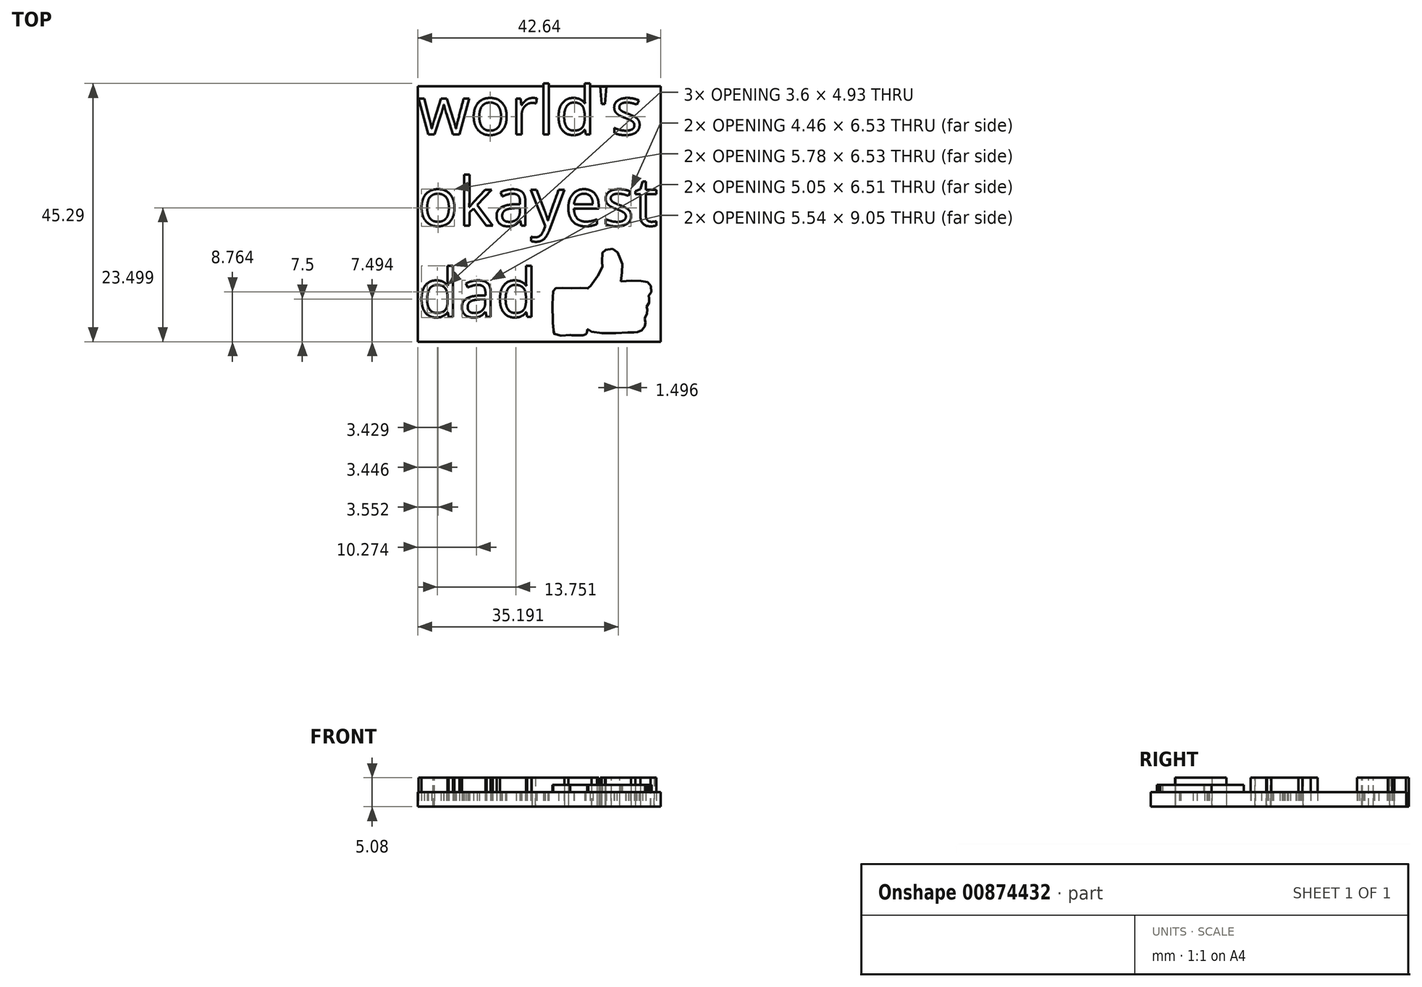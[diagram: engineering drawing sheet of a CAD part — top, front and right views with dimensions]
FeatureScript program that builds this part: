
annotation { "Feature Type Name" : "Feature", "Feature Type Description" : "" }
export const myFeature = defineFeature(function(context is Context, id is Id, definition is map)
    precondition{}
    {
        {
            var Q0;
            Q0=qCreatedBy(makeId("Top.planeOp"),FACE);
            var sketch = newSketch(context, id + "F0", { "sketchPlane" : qUnion([Q0])});
            skLineSegment(sketch, "E0.bottom", {"start": v(-21.32, 22.41) * mm, "end": v(21.32, 22.41) * mm});
            skLineSegment(sketch, "E0.top", {"start": v(-21.32, -22.41) * mm, "end": v(21.32, -22.41) * mm});
            skLineSegment(sketch, "E0.left", {"start": v(-21.32, 22.41) * mm, "end": v(-21.32, -22.41) * mm});
            skLineSegment(sketch, "E0.right", {"start": v(21.32, 22.41) * mm, "end": v(21.32, -22.41) * mm});
            skPoint(sketch, "E0.middle", {"position": v(0, 0) * mm});
            skText(sketch, "E1", { "text": "world\'s \nokayest \ndad", "fontName": "OpenSans-Regular.ttf"});
            const initialGuessF0  = {"E1": [-0.02132, 0.01394, 1, 0, 0.00847]};
            skSetInitialGuess(sketch, initialGuessF0);
            skSolve(sketch);
        }
        {
            var Q0;
            {var subQ5=sQuery(id+"F0.wireOp",EDGE,"E1.sketch_text.stroke-55");Q0=makeQuery(id+"F0.imprint","IMPRINT",FACE,{"disambiguationData":[TD([[makeQuery(id+"F0.imprint","IMPRINT",EDGE,{"derivedFrom":subQ5}),-1.0]])]});}
            var Q1;
            {var subQ5=sQuery(id+"F0.wireOp",EDGE,"E1.sketch_text.stroke-68");Q1=makeQuery(id+"F0.imprint","IMPRINT",FACE,{"disambiguationData":[TD([[makeQuery(id+"F0.imprint","IMPRINT",EDGE,{"derivedFrom":subQ5}),-1.0]])]});}
            var Q2;
            {var subQ5=sQuery(id+"F0.wireOp",EDGE,"E1.sketch_text.stroke-53");Q2=makeQuery(id+"F0.imprint","IMPRINT",FACE,{"disambiguationData":[TD([[makeQuery(id+"F0.imprint","IMPRINT",EDGE,{"derivedFrom":subQ5}),-1.0]])]});}
            var Q3;
            Q3=makeQuery(id+"F0.imprint","IMPRINT",FACE,{"disambiguationData":[TD([[makeQuery(id+"F0.imprint","IMPRINT",EDGE,{"derivedFrom":sQuery(id+"F0.wireOp",EDGE,"E1.sketch_text.stroke-57")}),-1.0]])]});
            var Q4;
            Q4=makeQuery(id+"F0.imprint","IMPRINT",FACE,{"disambiguationData":[TD([[makeQuery(id+"F0.imprint","IMPRINT",EDGE,{"derivedFrom":sQuery(id+"F0.wireOp",EDGE,"E1.sketch_text.stroke-40")}),-1.0]])]});
            var Q5;
            Q5=makeQuery(id+"F0.imprint","IMPRINT",FACE,{"disambiguationData":[TD([[makeQuery(id+"F0.imprint","IMPRINT",EDGE,{"derivedFrom":sQuery(id+"F0.wireOp",EDGE,"E1.sketch_text.stroke-23")}),-1.0]])]});
            var Q6;
            Q6=makeQuery(id+"F0.imprint","IMPRINT",FACE,{"disambiguationData":[TD([[makeQuery(id+"F0.imprint","IMPRINT",EDGE,{"derivedFrom":sQuery(id+"F0.wireOp",EDGE,"E1.sketch_text.stroke-0")}),-1.0]])]});
            var Q7;
            Q7=makeQuery(id+"F0.imprint","IMPRINT",FACE,{"disambiguationData":[TD([[makeQuery(id+"F0.imprint","IMPRINT",EDGE,{"derivedFrom":sQuery(id+"F0.wireOp",EDGE,"E1.sketch_text.stroke-81")}),-1.0]])]});
            var Q8;
            Q8=makeQuery(id+"F0.imprint","IMPRINT",FACE,{"disambiguationData":[TD([[makeQuery(id+"F0.imprint","IMPRINT",EDGE,{"derivedFrom":sQuery(id+"F0.wireOp",EDGE,"E1.sketch_text.stroke-85")}),-1.0]])]});
            extrude(context, id + "F1", {"entities" : qUnion([Q0, Q1, Q2, Q3, Q4, Q5, Q6, Q7, Q8]), "depth" : 5.08 * mm, "offsetDistance" : 25.4 * mm});
        }
        {
            var Q0;
            Q0=makeQuery(id+"F0.imprint","IMPRINT",FACE,{"disambiguationData":[TD([[makeQuery(id+"F0.imprint","IMPRINT",EDGE,{"derivedFrom":sQuery(id+"F0.wireOp",EDGE,"E1.sketch_text.stroke-110")}),-1.0]])]});
            var Q1;
            Q1=makeQuery(id+"F0.imprint","IMPRINT",FACE,{"disambiguationData":[TD([[makeQuery(id+"F0.imprint","IMPRINT",EDGE,{"derivedFrom":sQuery(id+"F0.wireOp",EDGE,"E1.sketch_text.stroke-127")}),-1.0]])]});
            var Q2;
            Q2=makeQuery(id+"F0.imprint","IMPRINT",FACE,{"disambiguationData":[TD([[makeQuery(id+"F0.imprint","IMPRINT",EDGE,{"derivedFrom":sQuery(id+"F0.wireOp",EDGE,"E1.sketch_text.stroke-142")}),-1.0]])]});
            var Q3;
            Q3=makeQuery(id+"F0.imprint","IMPRINT",FACE,{"disambiguationData":[TD([[makeQuery(id+"F0.imprint","IMPRINT",EDGE,{"derivedFrom":sQuery(id+"F0.wireOp",EDGE,"E1.sketch_text.stroke-169")}),-1.0]])]});
            var Q4;
            Q4=makeQuery(id+"F0.imprint","IMPRINT",FACE,{"disambiguationData":[TD([[makeQuery(id+"F0.imprint","IMPRINT",EDGE,{"derivedFrom":sQuery(id+"F0.wireOp",EDGE,"E1.sketch_text.stroke-185")}),-1.0]])]});
            var Q5;
            Q5=makeQuery(id+"F0.imprint","IMPRINT",FACE,{"disambiguationData":[TD([[makeQuery(id+"F0.imprint","IMPRINT",EDGE,{"derivedFrom":sQuery(id+"F0.wireOp",EDGE,"E1.sketch_text.stroke-204")}),-1.0]])]});
            var Q6;
            Q6=makeQuery(id+"F0.imprint","IMPRINT",FACE,{"disambiguationData":[TD([[makeQuery(id+"F0.imprint","IMPRINT",EDGE,{"derivedFrom":sQuery(id+"F0.wireOp",EDGE,"E1.sketch_text.stroke-229")}),-1.0]])]});
            extrude(context, id + "F2", {"entities" : qUnion([Q0, Q1, Q2, Q3, Q4, Q5, Q6]), "depth" : 5.08 * mm, "offsetDistance" : 25.4 * mm});
        }
        {
            var Q0;
            Q0=makeQuery(id+"F0.imprint","IMPRINT",FACE,{"disambiguationData":[TD([[makeQuery(id+"F0.imprint","IMPRINT",EDGE,{"derivedFrom":sQuery(id+"F0.wireOp",EDGE,"E1.sketch_text.stroke-248")}),-1.0]])]});
            var Q1;
            Q1=makeQuery(id+"F0.imprint","IMPRINT",FACE,{"disambiguationData":[TD([[makeQuery(id+"F0.imprint","IMPRINT",EDGE,{"derivedFrom":sQuery(id+"F0.wireOp",EDGE,"E1.sketch_text.stroke-272")}),-1.0]])]});
            var Q2;
            Q2=makeQuery(id+"F0.imprint","IMPRINT",FACE,{"disambiguationData":[TD([[makeQuery(id+"F0.imprint","IMPRINT",EDGE,{"derivedFrom":sQuery(id+"F0.wireOp",EDGE,"E1.sketch_text.stroke-299")}),-1.0]])]});
            extrude(context, id + "F3", {"entities" : qUnion([Q0, Q1, Q2]), "depth" : 5.08 * mm, "offsetDistance" : 25.4 * mm});
        }
        {
            var Q0;
            Q0=makeQuery(id+"F0.imprint","IMPRINT",FACE,{"disambiguationData":[TD([[makeQuery(id+"F0.imprint","IMPRINT",EDGE,{"derivedFrom":sQuery(id+"F0.wireOp",EDGE,"E0.top")}),1.0]])]});
            var Q1;
            Q1=makeQuery(id+"F0.imprint","IMPRINT",FACE,{"disambiguationData":[TD([[makeQuery(id+"F0.imprint","IMPRINT",EDGE,{"derivedFrom":sQuery(id+"F0.wireOp",EDGE,"E1.sketch_text.stroke-119")}),1.0]])]});
            var Q2;
            Q2=makeQuery(id+"F0.imprint","IMPRINT",FACE,{"disambiguationData":[TD([[makeQuery(id+"F0.imprint","IMPRINT",EDGE,{"derivedFrom":sQuery(id+"F0.wireOp",EDGE,"E1.sketch_text.stroke-161")}),1.0]])]});
            var Q3;
            Q3=makeQuery(id+"F0.imprint","IMPRINT",FACE,{"disambiguationData":[TD([[makeQuery(id+"F0.imprint","IMPRINT",EDGE,{"derivedFrom":sQuery(id+"F0.wireOp",EDGE,"E1.sketch_text.stroke-32")}),1.0]])]});
            var Q4;
            Q4=makeQuery(id+"F0.imprint","IMPRINT",FACE,{"disambiguationData":[TD([[makeQuery(id+"F0.imprint","IMPRINT",EDGE,{"derivedFrom":sQuery(id+"F0.wireOp",EDGE,"E1.sketch_text.stroke-72")}),1.0]])]});
            var Q5;
            Q5=makeQuery(id+"F0.imprint","IMPRINT",FACE,{"disambiguationData":[TD([[makeQuery(id+"F0.imprint","IMPRINT",EDGE,{"derivedFrom":sQuery(id+"F0.wireOp",EDGE,"E1.sketch_text.stroke-199")}),1.0]])]});
            var Q6;
            Q6=makeQuery(id+"F0.imprint","IMPRINT",FACE,{"disambiguationData":[TD([[makeQuery(id+"F0.imprint","IMPRINT",EDGE,{"derivedFrom":sQuery(id+"F0.wireOp",EDGE,"E1.sketch_text.stroke-314")}),1.0]])]});
            var Q7;
            Q7=makeQuery(id+"F0.imprint","IMPRINT",FACE,{"disambiguationData":[TD([[makeQuery(id+"F0.imprint","IMPRINT",EDGE,{"derivedFrom":sQuery(id+"F0.wireOp",EDGE,"E1.sketch_text.stroke-291")}),1.0]])]});
            var Q8;
            Q8=makeQuery(id+"F0.imprint","IMPRINT",FACE,{"disambiguationData":[TD([[makeQuery(id+"F0.imprint","IMPRINT",EDGE,{"derivedFrom":sQuery(id+"F0.wireOp",EDGE,"E1.sketch_text.stroke-263")}),1.0]])]});
            extrude(context, id + "F4", {"entities" : qUnion([Q0, Q1, Q2, Q3, Q4, Q5, Q6, Q7, Q8]), "depth" : 2.54 * mm, "offsetDistance" : 25.4 * mm});
        }
        {
            var Q0;
            Q0=makeQuery(id+"F4.opExtrude","CAP_FACE",FACE,{"disambiguationData":[OSD([sQuery(id+"F0.wireOp",EDGE,"E0.bottom"),sQuery(id+"F0.wireOp",EDGE,"E0.top"),sQuery(id+"F0.wireOp",EDGE,"E0.left"),sQuery(id+"F0.wireOp",EDGE,"E0.right"),sQuery(id+"F0.wireOp",EDGE,"E1.sketch_text.stroke-0"),sQuery(id+"F0.wireOp",EDGE,"E1.sketch_text.stroke-1"),sQuery(id+"F0.wireOp",EDGE,"E1.sketch_text.stroke-2"),sQuery(id+"F0.wireOp",EDGE,"E1.sketch_text.stroke-3"),sQuery(id+"F0.wireOp",EDGE,"E1.sketch_text.stroke-4"),sQuery(id+"F0.wireOp",EDGE,"E1.sketch_text.stroke-5"),sQuery(id+"F0.wireOp",EDGE,"E1.sketch_text.stroke-6"),sQuery(id+"F0.wireOp",EDGE,"E1.sketch_text.stroke-7"),sQuery(id+"F0.wireOp",EDGE,"E1.sketch_text.stroke-8"),sQuery(id+"F0.wireOp",EDGE,"E1.sketch_text.stroke-9"),sQuery(id+"F0.wireOp",EDGE,"E1.sketch_text.stroke-10"),sQuery(id+"F0.wireOp",EDGE,"E1.sketch_text.stroke-11"),sQuery(id+"F0.wireOp",EDGE,"E1.sketch_text.stroke-12"),sQuery(id+"F0.wireOp",EDGE,"E1.sketch_text.stroke-13"),sQuery(id+"F0.wireOp",EDGE,"E1.sketch_text.stroke-14"),sQuery(id+"F0.wireOp",EDGE,"E1.sketch_text.stroke-15"),sQuery(id+"F0.wireOp",EDGE,"E1.sketch_text.stroke-16"),sQuery(id+"F0.wireOp",EDGE,"E1.sketch_text.stroke-17"),sQuery(id+"F0.wireOp",EDGE,"E1.sketch_text.stroke-18"),sQuery(id+"F0.wireOp",EDGE,"E1.sketch_text.stroke-19"),sQuery(id+"F0.wireOp",EDGE,"E1.sketch_text.stroke-20"),sQuery(id+"F0.wireOp",EDGE,"E1.sketch_text.stroke-21"),sQuery(id+"F0.wireOp",EDGE,"E1.sketch_text.stroke-22"),sQuery(id+"F0.wireOp",EDGE,"E1.sketch_text.stroke-23"),sQuery(id+"F0.wireOp",EDGE,"E1.sketch_text.stroke-24"),sQuery(id+"F0.wireOp",EDGE,"E1.sketch_text.stroke-25"),sQuery(id+"F0.wireOp",EDGE,"E1.sketch_text.stroke-26"),sQuery(id+"F0.wireOp",EDGE,"E1.sketch_text.stroke-27"),sQuery(id+"F0.wireOp",EDGE,"E1.sketch_text.stroke-28"),sQuery(id+"F0.wireOp",EDGE,"E1.sketch_text.stroke-29"),sQuery(id+"F0.wireOp",EDGE,"E1.sketch_text.stroke-30"),sQuery(id+"F0.wireOp",EDGE,"E1.sketch_text.stroke-31"),sQuery(id+"F0.wireOp",EDGE,"E1.sketch_text.stroke-40"),sQuery(id+"F0.wireOp",EDGE,"E1.sketch_text.stroke-41"),sQuery(id+"F0.wireOp",EDGE,"E1.sketch_text.stroke-42"),sQuery(id+"F0.wireOp",EDGE,"E1.sketch_text.stroke-43"),sQuery(id+"F0.wireOp",EDGE,"E1.sketch_text.stroke-44"),sQuery(id+"F0.wireOp",EDGE,"E1.sketch_text.stroke-45"),sQuery(id+"F0.wireOp",EDGE,"E1.sketch_text.stroke-46"),sQuery(id+"F0.wireOp",EDGE,"E1.sketch_text.stroke-47"),sQuery(id+"F0.wireOp",EDGE,"E1.sketch_text.stroke-48"),sQuery(id+"F0.wireOp",EDGE,"E1.sketch_text.stroke-49"),sQuery(id+"F0.wireOp",EDGE,"E1.sketch_text.stroke-50"),sQuery(id+"F0.wireOp",EDGE,"E1.sketch_text.stroke-51"),sQuery(id+"F0.wireOp",EDGE,"E1.sketch_text.stroke-52"),sQuery(id+"F0.wireOp",EDGE,"E1.sketch_text.stroke-53"),sQuery(id+"F0.wireOp",EDGE,"E1.sketch_text.stroke-54"),sQuery(id+"F0.wireOp",EDGE,"E1.sketch_text.stroke-56"),sQuery(id+"F0.wireOp",EDGE,"E1.sketch_text.stroke-57"),sQuery(id+"F0.wireOp",EDGE,"E1.sketch_text.stroke-58"),sQuery(id+"F0.wireOp",EDGE,"E1.sketch_text.stroke-59"),sQuery(id+"F0.wireOp",EDGE,"E1.sketch_text.stroke-60"),sQuery(id+"F0.wireOp",EDGE,"E1.sketch_text.stroke-61"),sQuery(id+"F0.wireOp",EDGE,"E1.sketch_text.stroke-62"),sQuery(id+"F0.wireOp",EDGE,"E1.sketch_text.stroke-63"),sQuery(id+"F0.wireOp",EDGE,"E1.sketch_text.stroke-64"),sQuery(id+"F0.wireOp",EDGE,"E1.sketch_text.stroke-65"),sQuery(id+"F0.wireOp",EDGE,"E1.sketch_text.stroke-66"),sQuery(id+"F0.wireOp",EDGE,"E1.sketch_text.stroke-67"),sQuery(id+"F0.wireOp",EDGE,"E1.sketch_text.stroke-69"),sQuery(id+"F0.wireOp",EDGE,"E1.sketch_text.stroke-70"),sQuery(id+"F0.wireOp",EDGE,"E1.sketch_text.stroke-71"),sQuery(id+"F0.wireOp",EDGE,"E1.sketch_text.stroke-81"),sQuery(id+"F0.wireOp",EDGE,"E1.sketch_text.stroke-82"),sQuery(id+"F0.wireOp",EDGE,"E1.sketch_text.stroke-83"),sQuery(id+"F0.wireOp",EDGE,"E1.sketch_text.stroke-84"),sQuery(id+"F0.wireOp",EDGE,"E1.sketch_text.stroke-85"),sQuery(id+"F0.wireOp",EDGE,"E1.sketch_text.stroke-86"),sQuery(id+"F0.wireOp",EDGE,"E1.sketch_text.stroke-87"),sQuery(id+"F0.wireOp",EDGE,"E1.sketch_text.stroke-88"),sQuery(id+"F0.wireOp",EDGE,"E1.sketch_text.stroke-89"),sQuery(id+"F0.wireOp",EDGE,"E1.sketch_text.stroke-90"),sQuery(id+"F0.wireOp",EDGE,"E1.sketch_text.stroke-91"),sQuery(id+"F0.wireOp",EDGE,"E1.sketch_text.stroke-92"),sQuery(id+"F0.wireOp",EDGE,"E1.sketch_text.stroke-93"),sQuery(id+"F0.wireOp",EDGE,"E1.sketch_text.stroke-94"),sQuery(id+"F0.wireOp",EDGE,"E1.sketch_text.stroke-95"),sQuery(id+"F0.wireOp",EDGE,"E1.sketch_text.stroke-96"),sQuery(id+"F0.wireOp",EDGE,"E1.sketch_text.stroke-97"),sQuery(id+"F0.wireOp",EDGE,"E1.sketch_text.stroke-98"),sQuery(id+"F0.wireOp",EDGE,"E1.sketch_text.stroke-99"),sQuery(id+"F0.wireOp",EDGE,"E1.sketch_text.stroke-100"),sQuery(id+"F0.wireOp",EDGE,"E1.sketch_text.stroke-101"),sQuery(id+"F0.wireOp",EDGE,"E1.sketch_text.stroke-102"),sQuery(id+"F0.wireOp",EDGE,"E1.sketch_text.stroke-103"),sQuery(id+"F0.wireOp",EDGE,"E1.sketch_text.stroke-104"),sQuery(id+"F0.wireOp",EDGE,"E1.sketch_text.stroke-105"),sQuery(id+"F0.wireOp",EDGE,"E1.sketch_text.stroke-106"),sQuery(id+"F0.wireOp",EDGE,"E1.sketch_text.stroke-107"),sQuery(id+"F0.wireOp",EDGE,"E1.sketch_text.stroke-108"),sQuery(id+"F0.wireOp",EDGE,"E1.sketch_text.stroke-109"),sQuery(id+"F0.wireOp",EDGE,"E1.sketch_text.stroke-110"),sQuery(id+"F0.wireOp",EDGE,"E1.sketch_text.stroke-111"),sQuery(id+"F0.wireOp",EDGE,"E1.sketch_text.stroke-112"),sQuery(id+"F0.wireOp",EDGE,"E1.sketch_text.stroke-113"),sQuery(id+"F0.wireOp",EDGE,"E1.sketch_text.stroke-114"),sQuery(id+"F0.wireOp",EDGE,"E1.sketch_text.stroke-115"),sQuery(id+"F0.wireOp",EDGE,"E1.sketch_text.stroke-116"),sQuery(id+"F0.wireOp",EDGE,"E1.sketch_text.stroke-117"),sQuery(id+"F0.wireOp",EDGE,"E1.sketch_text.stroke-118"),sQuery(id+"F0.wireOp",EDGE,"E1.sketch_text.stroke-127"),sQuery(id+"F0.wireOp",EDGE,"E1.sketch_text.stroke-128"),sQuery(id+"F0.wireOp",EDGE,"E1.sketch_text.stroke-129"),sQuery(id+"F0.wireOp",EDGE,"E1.sketch_text.stroke-130"),sQuery(id+"F0.wireOp",EDGE,"E1.sketch_text.stroke-131"),sQuery(id+"F0.wireOp",EDGE,"E1.sketch_text.stroke-132"),sQuery(id+"F0.wireOp",EDGE,"E1.sketch_text.stroke-133"),sQuery(id+"F0.wireOp",EDGE,"E1.sketch_text.stroke-134"),sQuery(id+"F0.wireOp",EDGE,"E1.sketch_text.stroke-135"),sQuery(id+"F0.wireOp",EDGE,"E1.sketch_text.stroke-136"),sQuery(id+"F0.wireOp",EDGE,"E1.sketch_text.stroke-137"),sQuery(id+"F0.wireOp",EDGE,"E1.sketch_text.stroke-138"),sQuery(id+"F0.wireOp",EDGE,"E1.sketch_text.stroke-139"),sQuery(id+"F0.wireOp",EDGE,"E1.sketch_text.stroke-140"),sQuery(id+"F0.wireOp",EDGE,"E1.sketch_text.stroke-141"),sQuery(id+"F0.wireOp",EDGE,"E1.sketch_text.stroke-142"),sQuery(id+"F0.wireOp",EDGE,"E1.sketch_text.stroke-143"),sQuery(id+"F0.wireOp",EDGE,"E1.sketch_text.stroke-144"),sQuery(id+"F0.wireOp",EDGE,"E1.sketch_text.stroke-145"),sQuery(id+"F0.wireOp",EDGE,"E1.sketch_text.stroke-146"),sQuery(id+"F0.wireOp",EDGE,"E1.sketch_text.stroke-147"),sQuery(id+"F0.wireOp",EDGE,"E1.sketch_text.stroke-148"),sQuery(id+"F0.wireOp",EDGE,"E1.sketch_text.stroke-149"),sQuery(id+"F0.wireOp",EDGE,"E1.sketch_text.stroke-150"),sQuery(id+"F0.wireOp",EDGE,"E1.sketch_text.stroke-151"),sQuery(id+"F0.wireOp",EDGE,"E1.sketch_text.stroke-152"),sQuery(id+"F0.wireOp",EDGE,"E1.sketch_text.stroke-153"),sQuery(id+"F0.wireOp",EDGE,"E1.sketch_text.stroke-154"),sQuery(id+"F0.wireOp",EDGE,"E1.sketch_text.stroke-155"),sQuery(id+"F0.wireOp",EDGE,"E1.sketch_text.stroke-156"),sQuery(id+"F0.wireOp",EDGE,"E1.sketch_text.stroke-157"),sQuery(id+"F0.wireOp",EDGE,"E1.sketch_text.stroke-158"),sQuery(id+"F0.wireOp",EDGE,"E1.sketch_text.stroke-159"),sQuery(id+"F0.wireOp",EDGE,"E1.sketch_text.stroke-160"),sQuery(id+"F0.wireOp",EDGE,"E1.sketch_text.stroke-169"),sQuery(id+"F0.wireOp",EDGE,"E1.sketch_text.stroke-170"),sQuery(id+"F0.wireOp",EDGE,"E1.sketch_text.stroke-171"),sQuery(id+"F0.wireOp",EDGE,"E1.sketch_text.stroke-172"),sQuery(id+"F0.wireOp",EDGE,"E1.sketch_text.stroke-173"),sQuery(id+"F0.wireOp",EDGE,"E1.sketch_text.stroke-174"),sQuery(id+"F0.wireOp",EDGE,"E1.sketch_text.stroke-175"),sQuery(id+"F0.wireOp",EDGE,"E1.sketch_text.stroke-176"),sQuery(id+"F0.wireOp",EDGE,"E1.sketch_text.stroke-177"),sQuery(id+"F0.wireOp",EDGE,"E1.sketch_text.stroke-178"),sQuery(id+"F0.wireOp",EDGE,"E1.sketch_text.stroke-179"),sQuery(id+"F0.wireOp",EDGE,"E1.sketch_text.stroke-180"),sQuery(id+"F0.wireOp",EDGE,"E1.sketch_text.stroke-181"),sQuery(id+"F0.wireOp",EDGE,"E1.sketch_text.stroke-182"),sQuery(id+"F0.wireOp",EDGE,"E1.sketch_text.stroke-183"),sQuery(id+"F0.wireOp",EDGE,"E1.sketch_text.stroke-184"),sQuery(id+"F0.wireOp",EDGE,"E1.sketch_text.stroke-185"),sQuery(id+"F0.wireOp",EDGE,"E1.sketch_text.stroke-186"),sQuery(id+"F0.wireOp",EDGE,"E1.sketch_text.stroke-187"),sQuery(id+"F0.wireOp",EDGE,"E1.sketch_text.stroke-188"),sQuery(id+"F0.wireOp",EDGE,"E1.sketch_text.stroke-189"),sQuery(id+"F0.wireOp",EDGE,"E1.sketch_text.stroke-190"),sQuery(id+"F0.wireOp",EDGE,"E1.sketch_text.stroke-191"),sQuery(id+"F0.wireOp",EDGE,"E1.sketch_text.stroke-192"),sQuery(id+"F0.wireOp",EDGE,"E1.sketch_text.stroke-193"),sQuery(id+"F0.wireOp",EDGE,"E1.sketch_text.stroke-194"),sQuery(id+"F0.wireOp",EDGE,"E1.sketch_text.stroke-195"),sQuery(id+"F0.wireOp",EDGE,"E1.sketch_text.stroke-196"),sQuery(id+"F0.wireOp",EDGE,"E1.sketch_text.stroke-197"),sQuery(id+"F0.wireOp",EDGE,"E1.sketch_text.stroke-198"),sQuery(id+"F0.wireOp",EDGE,"E1.sketch_text.stroke-204"),sQuery(id+"F0.wireOp",EDGE,"E1.sketch_text.stroke-205"),sQuery(id+"F0.wireOp",EDGE,"E1.sketch_text.stroke-206"),sQuery(id+"F0.wireOp",EDGE,"E1.sketch_text.stroke-207"),sQuery(id+"F0.wireOp",EDGE,"E1.sketch_text.stroke-208"),sQuery(id+"F0.wireOp",EDGE,"E1.sketch_text.stroke-209"),sQuery(id+"F0.wireOp",EDGE,"E1.sketch_text.stroke-210"),sQuery(id+"F0.wireOp",EDGE,"E1.sketch_text.stroke-211"),sQuery(id+"F0.wireOp",EDGE,"E1.sketch_text.stroke-212"),sQuery(id+"F0.wireOp",EDGE,"E1.sketch_text.stroke-213"),sQuery(id+"F0.wireOp",EDGE,"E1.sketch_text.stroke-214"),sQuery(id+"F0.wireOp",EDGE,"E1.sketch_text.stroke-215"),sQuery(id+"F0.wireOp",EDGE,"E1.sketch_text.stroke-216"),sQuery(id+"F0.wireOp",EDGE,"E1.sketch_text.stroke-217"),sQuery(id+"F0.wireOp",EDGE,"E1.sketch_text.stroke-218"),sQuery(id+"F0.wireOp",EDGE,"E1.sketch_text.stroke-219"),sQuery(id+"F0.wireOp",EDGE,"E1.sketch_text.stroke-220"),sQuery(id+"F0.wireOp",EDGE,"E1.sketch_text.stroke-221"),sQuery(id+"F0.wireOp",EDGE,"E1.sketch_text.stroke-222"),sQuery(id+"F0.wireOp",EDGE,"E1.sketch_text.stroke-223"),sQuery(id+"F0.wireOp",EDGE,"E1.sketch_text.stroke-224"),sQuery(id+"F0.wireOp",EDGE,"E1.sketch_text.stroke-225"),sQuery(id+"F0.wireOp",EDGE,"E1.sketch_text.stroke-226"),sQuery(id+"F0.wireOp",EDGE,"E1.sketch_text.stroke-227"),sQuery(id+"F0.wireOp",EDGE,"E1.sketch_text.stroke-228"),sQuery(id+"F0.wireOp",EDGE,"E1.sketch_text.stroke-229"),sQuery(id+"F0.wireOp",EDGE,"E1.sketch_text.stroke-230"),sQuery(id+"F0.wireOp",EDGE,"E1.sketch_text.stroke-231"),sQuery(id+"F0.wireOp",EDGE,"E1.sketch_text.stroke-232"),sQuery(id+"F0.wireOp",EDGE,"E1.sketch_text.stroke-233"),sQuery(id+"F0.wireOp",EDGE,"E1.sketch_text.stroke-234"),sQuery(id+"F0.wireOp",EDGE,"E1.sketch_text.stroke-235"),sQuery(id+"F0.wireOp",EDGE,"E1.sketch_text.stroke-236"),sQuery(id+"F0.wireOp",EDGE,"E1.sketch_text.stroke-237"),sQuery(id+"F0.wireOp",EDGE,"E1.sketch_text.stroke-238"),sQuery(id+"F0.wireOp",EDGE,"E1.sketch_text.stroke-239"),sQuery(id+"F0.wireOp",EDGE,"E1.sketch_text.stroke-240"),sQuery(id+"F0.wireOp",EDGE,"E1.sketch_text.stroke-241"),sQuery(id+"F0.wireOp",EDGE,"E1.sketch_text.stroke-242"),sQuery(id+"F0.wireOp",EDGE,"E1.sketch_text.stroke-243"),sQuery(id+"F0.wireOp",EDGE,"E1.sketch_text.stroke-244"),sQuery(id+"F0.wireOp",EDGE,"E1.sketch_text.stroke-245"),sQuery(id+"F0.wireOp",EDGE,"E1.sketch_text.stroke-246"),sQuery(id+"F0.wireOp",EDGE,"E1.sketch_text.stroke-247"),sQuery(id+"F0.wireOp",EDGE,"E1.sketch_text.stroke-248"),sQuery(id+"F0.wireOp",EDGE,"E1.sketch_text.stroke-249"),sQuery(id+"F0.wireOp",EDGE,"E1.sketch_text.stroke-250"),sQuery(id+"F0.wireOp",EDGE,"E1.sketch_text.stroke-251"),sQuery(id+"F0.wireOp",EDGE,"E1.sketch_text.stroke-252"),sQuery(id+"F0.wireOp",EDGE,"E1.sketch_text.stroke-253"),sQuery(id+"F0.wireOp",EDGE,"E1.sketch_text.stroke-254"),sQuery(id+"F0.wireOp",EDGE,"E1.sketch_text.stroke-255"),sQuery(id+"F0.wireOp",EDGE,"E1.sketch_text.stroke-256"),sQuery(id+"F0.wireOp",EDGE,"E1.sketch_text.stroke-257"),sQuery(id+"F0.wireOp",EDGE,"E1.sketch_text.stroke-258"),sQuery(id+"F0.wireOp",EDGE,"E1.sketch_text.stroke-259"),sQuery(id+"F0.wireOp",EDGE,"E1.sketch_text.stroke-260"),sQuery(id+"F0.wireOp",EDGE,"E1.sketch_text.stroke-261"),sQuery(id+"F0.wireOp",EDGE,"E1.sketch_text.stroke-262"),sQuery(id+"F0.wireOp",EDGE,"E1.sketch_text.stroke-272"),sQuery(id+"F0.wireOp",EDGE,"E1.sketch_text.stroke-273"),sQuery(id+"F0.wireOp",EDGE,"E1.sketch_text.stroke-274"),sQuery(id+"F0.wireOp",EDGE,"E1.sketch_text.stroke-275"),sQuery(id+"F0.wireOp",EDGE,"E1.sketch_text.stroke-276"),sQuery(id+"F0.wireOp",EDGE,"E1.sketch_text.stroke-277"),sQuery(id+"F0.wireOp",EDGE,"E1.sketch_text.stroke-278"),sQuery(id+"F0.wireOp",EDGE,"E1.sketch_text.stroke-279"),sQuery(id+"F0.wireOp",EDGE,"E1.sketch_text.stroke-280"),sQuery(id+"F0.wireOp",EDGE,"E1.sketch_text.stroke-281"),sQuery(id+"F0.wireOp",EDGE,"E1.sketch_text.stroke-282"),sQuery(id+"F0.wireOp",EDGE,"E1.sketch_text.stroke-283"),sQuery(id+"F0.wireOp",EDGE,"E1.sketch_text.stroke-284"),sQuery(id+"F0.wireOp",EDGE,"E1.sketch_text.stroke-285"),sQuery(id+"F0.wireOp",EDGE,"E1.sketch_text.stroke-286"),sQuery(id+"F0.wireOp",EDGE,"E1.sketch_text.stroke-287"),sQuery(id+"F0.wireOp",EDGE,"E1.sketch_text.stroke-288"),sQuery(id+"F0.wireOp",EDGE,"E1.sketch_text.stroke-289"),sQuery(id+"F0.wireOp",EDGE,"E1.sketch_text.stroke-290"),sQuery(id+"F0.wireOp",EDGE,"E1.sketch_text.stroke-299"),sQuery(id+"F0.wireOp",EDGE,"E1.sketch_text.stroke-300"),sQuery(id+"F0.wireOp",EDGE,"E1.sketch_text.stroke-301"),sQuery(id+"F0.wireOp",EDGE,"E1.sketch_text.stroke-302"),sQuery(id+"F0.wireOp",EDGE,"E1.sketch_text.stroke-303"),sQuery(id+"F0.wireOp",EDGE,"E1.sketch_text.stroke-304"),sQuery(id+"F0.wireOp",EDGE,"E1.sketch_text.stroke-305"),sQuery(id+"F0.wireOp",EDGE,"E1.sketch_text.stroke-306"),sQuery(id+"F0.wireOp",EDGE,"E1.sketch_text.stroke-307"),sQuery(id+"F0.wireOp",EDGE,"E1.sketch_text.stroke-308"),sQuery(id+"F0.wireOp",EDGE,"E1.sketch_text.stroke-309"),sQuery(id+"F0.wireOp",EDGE,"E1.sketch_text.stroke-310"),sQuery(id+"F0.wireOp",EDGE,"E1.sketch_text.stroke-311"),sQuery(id+"F0.wireOp",EDGE,"E1.sketch_text.stroke-312"),sQuery(id+"F0.wireOp",EDGE,"E1.sketch_text.stroke-313")])],"isStart":false});
            var sketch = newSketch(context, id + "F5", { "sketchPlane" : qUnion([Q0])});
            skFitSpline(sketch, "E2", {"points": [v(5.43, -21.25) * mm, v(3.22, -21.28) * mm, v(2.43, -20.83) * mm, v(2.48, -20.43) * mm, v(2.45, -20.14) * mm, v(2.43, -13.62) * mm, v(2.61, -13.27) * mm, v(3.06, -12.96) * mm, v(4.93, -13.06) * mm, v(7.09, -12.96) * mm, v(8.5, -13.04) * mm, v(8.54, -13.06) * mm, v(9.06, -12.56) * mm, v(11.09, -9.35) * mm, v(11.04, -8.96) * mm, v(11.06, -6.85) * mm, v(11.22, -6.61) * mm, v(12.12, -6.09) * mm, v(13.4, -6.4) * mm, v(13.93, -7.17) * mm, v(14.46, -8.46) * mm, v(14.62, -9.3) * mm, v(14.3, -11.8) * mm, v(14.3, -11.83) * mm], "startDerivative": vector(-38.72, -3.6) * mm, "endDerivative": vector(0.4, -1.74) * mm});
            skFitSpline(sketch, "E3", {"points": [v(14.3, -11.8) * mm, v(18.38, -11.8) * mm, v(19.49, -12.43) * mm, v(19.6, -13.88) * mm, v(19.17, -14.35) * mm, v(19.27, -14.84) * mm, v(19.23, -15.66) * mm, v(18.8, -16.34) * mm, v(18.85, -16.48) * mm, v(18.96, -17.2) * mm, v(18.66, -18.05) * mm, v(18.46, -18.25) * mm, v(18.47, -18.31) * mm, v(18.57, -18.54) * mm, v(18.6, -19.29) * mm, v(18.36, -19.93) * mm, v(17.57, -20.64) * mm, v(16.82, -20.78) * mm, v(15.98, -20.77) * mm, v(9.58, -20.77) * mm, v(8.56, -20.3) * mm, v(8.58, -20.3) * mm], "startDerivative": vector(44.74, 2.2) * mm, "endDerivative": vector(2.7, -0.5) * mm});
            skFitSpline(sketch, "E4", {"points": [v(8.58, -20.3) * mm, v(8.4, -20.3) * mm, v(8.4, -20.32) * mm, v(8.38, -20.7) * mm, v(8.18, -21.1) * mm, v(7.76, -21.26) * mm, v(5.43, -21.25) * mm], "startDerivative": vector(-2.24, 0.17) * mm, "endDerivative": vector(-7.45, 0.3) * mm});
            skSolve(sketch);
        }
        {
            var Q0;
            Q0 = qSketchRegion(id + "F5", true);
            extrude(context, id + "F6", {"entities" : qUnion([Q0]), "operationType" : NewBodyOperationType.ADD, "depth" : 1.27 * mm, "offsetDistance" : 25.4 * mm});
        }
    });
